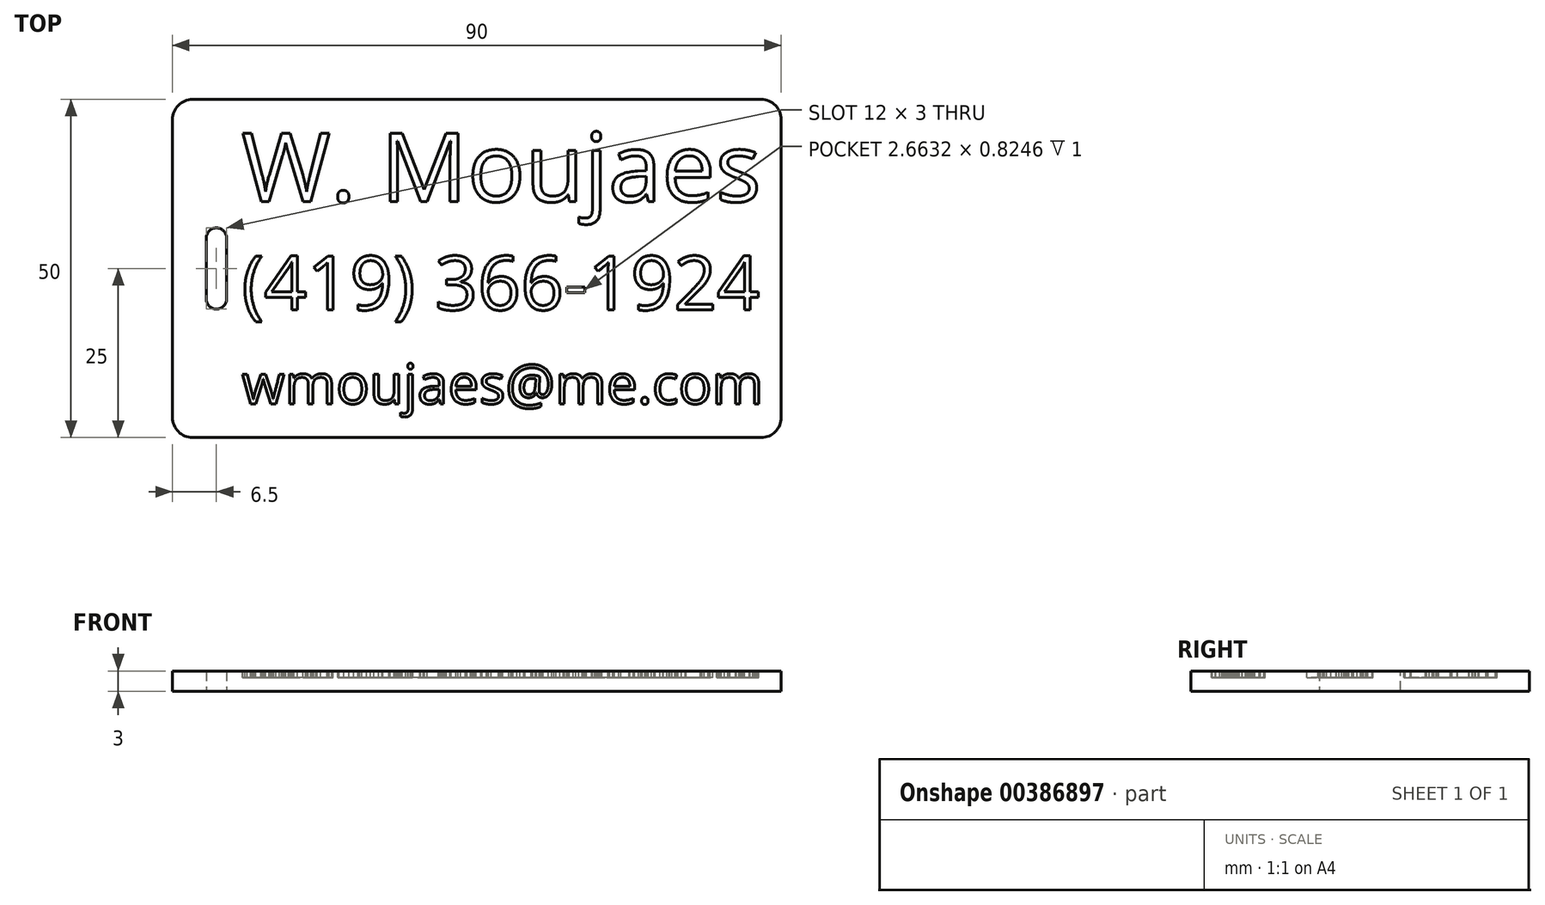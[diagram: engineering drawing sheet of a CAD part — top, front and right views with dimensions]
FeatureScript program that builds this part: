
annotation { "Feature Type Name" : "Feature", "Feature Type Description" : "" }
export const myFeature = defineFeature(function(context is Context, id is Id, definition is map)
    precondition{}
    {
        {
            var Q0;
            Q0=qCreatedBy(makeId("Top.planeOp"),FACE);
            var sketch = newSketch(context, id + "F0", { "sketchPlane" : qUnion([Q0])});
            skLineSegment(sketch, "E0.bottom", {"start": v(3, 0) * mm, "end": v(87, 0) * mm});
            skLineSegment(sketch, "E0.top", {"start": v(3, 50) * mm, "end": v(87, 50) * mm});
            skLineSegment(sketch, "E0.left", {"start": v(0, 3) * mm, "end": v(0, 47) * mm});
            skLineSegment(sketch, "E0.right", {"start": v(90, 3) * mm, "end": v(90, 47) * mm});
            skPoint(sketch, "E1.visualSharp", {"position": v(0, 50) * mm});
            skArc(sketch, "E1.filletArc", {"start": v(3, 50) * mm, "mid": v(0.88, 49.12) * mm, "end": v(0, 47) * mm});
            skPoint(sketch, "E2.visualSharp", {"position": v(90, 50) * mm});
            skArc(sketch, "E2.filletArc", {"start": v(90, 47) * mm, "mid": v(89.12, 49.12) * mm, "end": v(87, 50) * mm});
            skPoint(sketch, "E3.visualSharp", {"position": v(90, 0) * mm});
            skArc(sketch, "E3.filletArc", {"start": v(87, 0) * mm, "mid": v(89.12, 0.88) * mm, "end": v(90, 3) * mm});
            skPoint(sketch, "E4.visualSharp", {"position": v(0, 0) * mm});
            skArc(sketch, "E4.filletArc", {"start": v(0, 3) * mm, "mid": v(0.88, 0.88) * mm, "end": v(3, 0) * mm});
            skLineSegment(sketch, "E5.bottom", {"start": v(8, 31) * mm, "end": v(5, 31) * mm});
            skLineSegment(sketch, "E5.top", {"start": v(8, 19) * mm, "end": v(5, 19) * mm});
            skLineSegment(sketch, "E5.left", {"start": v(8, 31) * mm, "end": v(8, 19) * mm});
            skLineSegment(sketch, "E5.right", {"start": v(5, 31) * mm, "end": v(5, 19) * mm});
            skPoint(sketch, "E5.middle", {"position": v(6.5, 25) * mm});
            skPoint(sketch, "E5.middle.positionSnap0", {"position": v(0, 25) * mm});
            skPoint(sketch, "E5.centerSnap0", {"position": v(0, 25) * mm});
            skSolve(sketch);
        }
        {
            var Q0;
            Q0 = qSketchRegion(id + "F0", true);
            extrude(context, id + "F1", {"entities" : qUnion([Q0]), "depth" : 3 * mm});
        }
        {
            var Q0;
            Q0=makeQuery(id+"F1.opExtrude","SWEPT_EDGE",EDGE,{"disambiguationData":[OSD([sQuery(id+"F0.wireOp",EDGE,"E5.bottom"),sQuery(id+"F0.wireOp",EDGE,"E5.right")])]});
            var Q1;
            Q1=makeQuery(id+"F1.opExtrude","SWEPT_EDGE",EDGE,{"disambiguationData":[OSD([sQuery(id+"F0.wireOp",EDGE,"E5.bottom"),sQuery(id+"F0.wireOp",EDGE,"E5.left")])]});
            var Q2;
            Q2=makeQuery(id+"F1.opExtrude","SWEPT_EDGE",EDGE,{"disambiguationData":[OSD([sQuery(id+"F0.wireOp",EDGE,"E5.top"),sQuery(id+"F0.wireOp",EDGE,"E5.right")])]});
            var Q3;
            Q3=makeQuery(id+"F1.opExtrude","SWEPT_EDGE",EDGE,{"disambiguationData":[OSD([sQuery(id+"F0.wireOp",EDGE,"E5.top"),sQuery(id+"F0.wireOp",EDGE,"E5.left")])]});
            fillet(context, id + "F2", {"entities" : qUnion([Q0, Q1, Q2, Q3]), "radius" : 1.5 * mm, "tangentPropagation" : true, "allowEdgeOverflow" : false});
        }
        {
            var Q0;
            Q0=makeQuery(id+"F1.opExtrude","CAP_FACE",FACE,{"disambiguationData":[OSD([sQuery(id+"F0.wireOp",EDGE,"E0.bottom"),sQuery(id+"F0.wireOp",EDGE,"E0.top"),sQuery(id+"F0.wireOp",EDGE,"E0.left"),sQuery(id+"F0.wireOp",EDGE,"E0.right"),sQuery(id+"F0.wireOp",EDGE,"E1.filletArc"),sQuery(id+"F0.wireOp",EDGE,"E2.filletArc"),sQuery(id+"F0.wireOp",EDGE,"E3.filletArc"),sQuery(id+"F0.wireOp",EDGE,"E4.filletArc"),sQuery(id+"F0.wireOp",EDGE,"E5.bottom"),sQuery(id+"F0.wireOp",EDGE,"E5.top"),sQuery(id+"F0.wireOp",EDGE,"E5.left"),sQuery(id+"F0.wireOp",EDGE,"E5.right")])],"isStart":false});
            var sketch = newSketch(context, id + "F3", { "sketchPlane" : qUnion([Q0])});
            skText(sketch, "E6", { "text": "W. Moujaes", "fontName": "OpenSans-Regular.ttf"});
            skText(sketch, "E7", { "text": "(419) 366-1924", "fontName": "OpenSans-Regular.ttf"});
            skText(sketch, "E8", { "text": "<email>", "fontName": "OpenSans-Regular.ttf"});
            const initialGuessF3  = {"E6": [0.01025, 0.03488, 1, 0, 0.0102], "E7": [0.01025, 0.01888, 1, 0, 0.008], "E8": [0.01025, 0.005, 1, 0, 0.00588]};
            skSetInitialGuess(sketch, initialGuessF3);
            skSolve(sketch);
        }
        {
            var Q0;
            Q0 = qSketchRegion(id + "F3", true);
            extrude(context, id + "F4", {"entities" : qUnion([Q0]), "operationType" : NewBodyOperationType.REMOVE, "oppositeDirection" : true, "depth" : 1 * mm});
        }
    });
